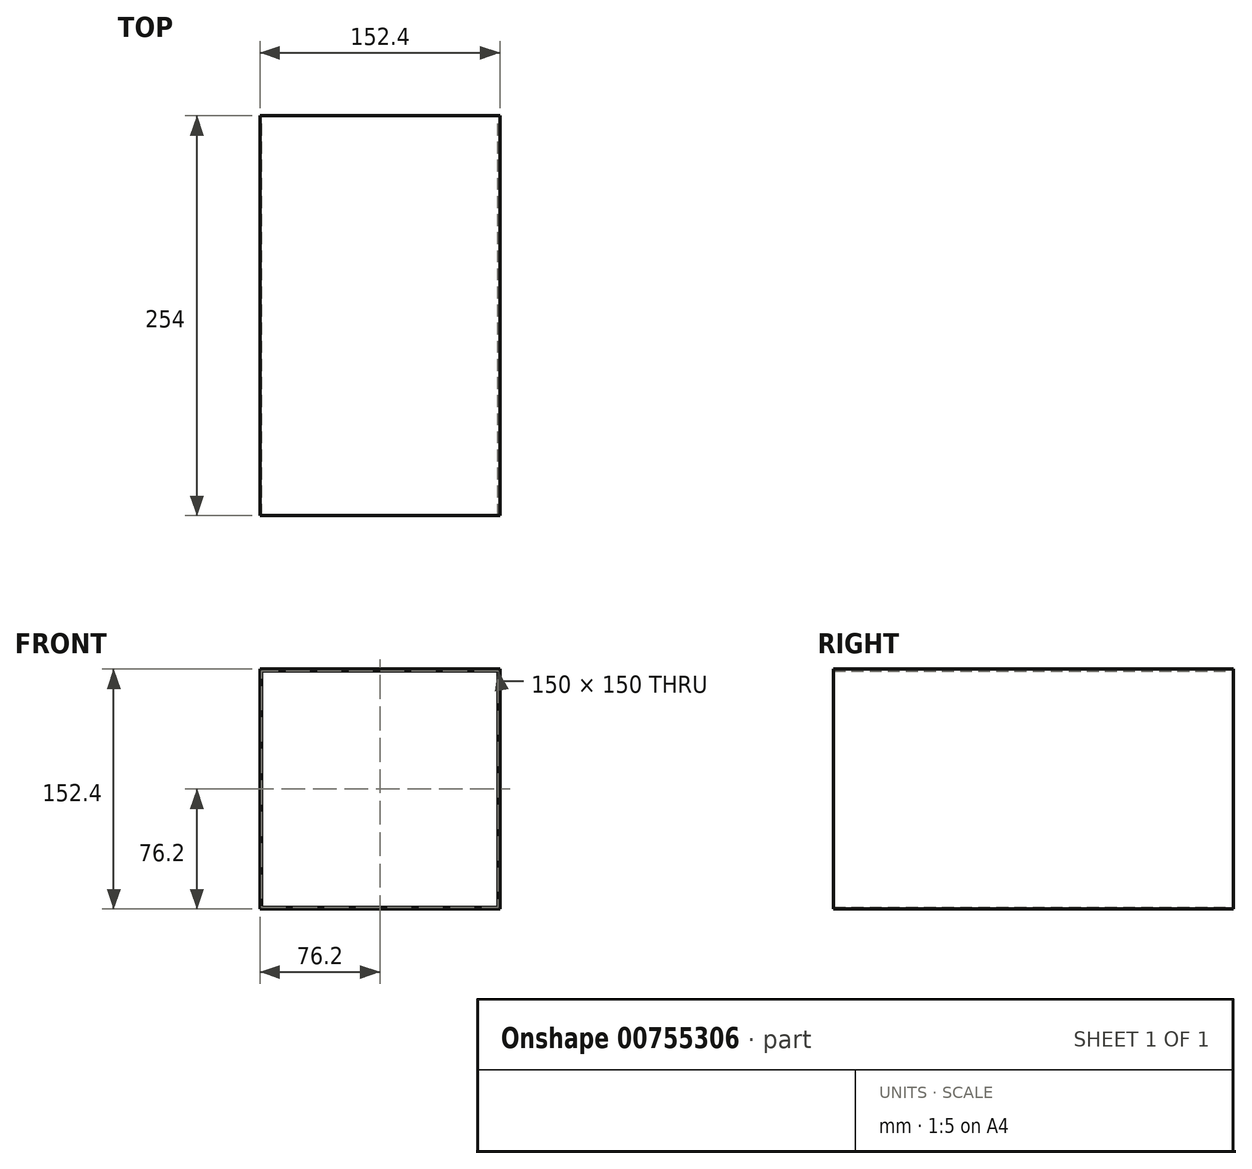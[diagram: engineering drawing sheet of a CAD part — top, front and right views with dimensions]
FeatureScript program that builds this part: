
annotation { "Feature Type Name" : "Feature", "Feature Type Description" : "" }
export const myFeature = defineFeature(function(context is Context, id is Id, definition is map)
    precondition{}
    {
        {
            var Q0;
            Q0=qCreatedBy(makeId("Front.planeOp"),FACE);
            var sketch = newSketch(context, id + "F0", { "sketchPlane" : qUnion([Q0])});
            skLineSegment(sketch, "E0.bottom", {"start": v(76.2, 76.2) * mm, "end": v(-76.2, 76.2) * mm});
            skLineSegment(sketch, "E0.top", {"start": v(76.2, -76.2) * mm, "end": v(-76.2, -76.2) * mm});
            skLineSegment(sketch, "E0.left", {"start": v(76.2, 76.2) * mm, "end": v(76.2, -76.2) * mm});
            skLineSegment(sketch, "E0.right", {"start": v(-76.2, 76.2) * mm, "end": v(-76.2, -76.2) * mm});
            skPoint(sketch, "E0.middle", {"position": v(0, 0) * mm});
            skLineSegment(sketch, "E1.bottom", {"start": v(75, 75) * mm, "end": v(-75, 75) * mm});
            skLineSegment(sketch, "E1.top", {"start": v(75, -75) * mm, "end": v(-75, -75) * mm});
            skLineSegment(sketch, "E1.left", {"start": v(75, 75) * mm, "end": v(75, -75) * mm});
            skLineSegment(sketch, "E1.right", {"start": v(-75, 75) * mm, "end": v(-75, -75) * mm});
            skSolve(sketch);
        }
        {
            var Q0;
            Q0=makeQuery(id+"F0.imprint","IMPRINT",FACE,{"disambiguationData":[TD([[makeQuery(id+"F0.imprint","IMPRINT",EDGE,{"derivedFrom":sQuery(id+"F0.wireOp",EDGE,"E0.bottom")}),1.0]])]});
            extrude(context, id + "F1", {"entities" : qUnion([Q0]), "depth" : 254 * mm, "offsetDistance" : 25 * mm});
        }
    });
